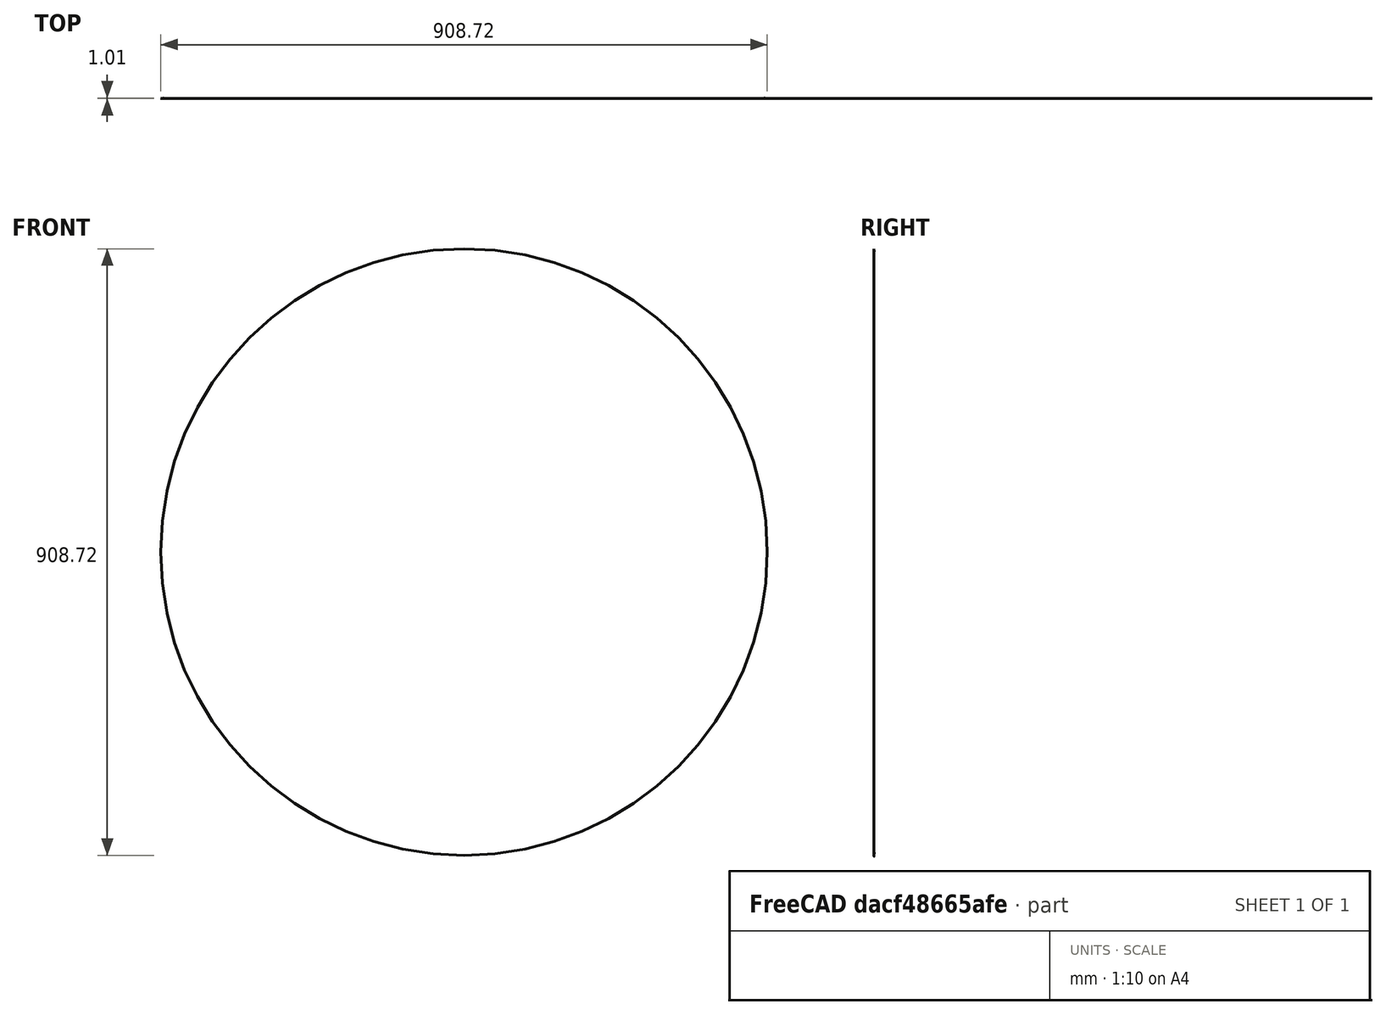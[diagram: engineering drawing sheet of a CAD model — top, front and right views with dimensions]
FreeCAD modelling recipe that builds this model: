
FCSTD DOCUMENT  (FreeCAD 0.18R16117 (Git))
Label: dish_with_rim
License: All rights reserved
LicenseURL: http://en.wikipedia.org/wiki/All_rights_reserved
objects: Sketcher::SketchObject×1, PartDesign::Revolution×1, PartDesign::Body×1, App::Part×1
note: 4 computed .brp shape members not serialized (recipe doc carries the construction recipe); baked Part::Feature solids carry a one-line shape summary decoded from their .brp

FEATURE [Sketcher::SketchObject] Sketch
  MapMode = 5
  Placement = pos=(0,0,0) rot=(0.57735,0.57735,0.57735;2.0944rad)
  Support = -> [YZ_Plane001]
  expr: Constraints[19] = Constraints.thickness
  sketch-geometry (13):
    g0: GeomPoint X=-337.5 Y=0 Z=0
    g1: ArcOfParabola CenterX=0 CenterY=0 CenterZ=0 NormalX=0 NormalY=0 NormalZ=1 Focal=337.5 AngleXU=-3.14159 StartAngle=-450 EndAngle=0
    g2: GeomPoint X=-337.5 Y=0 Z=0
    g3: LineSegment [constr] StartX=0 StartY=0 StartZ=0 EndX=-337.5 EndY=0 EndZ=0
    g4: Circle [constr] CenterX=-145.008 CenterY=453.328 CenterZ=0 NormalX=0 NormalY=0 NormalZ=1 AngleXU=0 Radius=6
    g5: GeomPoint X=-150 Y=450 Z=0
    g6: ArcOfParabola CenterX=2 CenterY=0 CenterZ=0 NormalX=0 NormalY=0 NormalZ=1 Focal=337.5 AngleXU=-3.14159 StartAngle=-454.357 EndAngle=0
    g7: GeomPoint X=-335.5 Y=0 Z=0
    g8: LineSegment [constr] StartX=2 StartY=0 StartZ=0 EndX=-335.5 EndY=0 EndZ=0
    g9: LineSegment StartX=0 StartY=0 StartZ=0 EndX=2 EndY=0 EndZ=0
    g10: GeomPoint X=-150.919 Y=454.357 Z=0
    g11: GeomPoint X=-150.919 Y=454.357 Z=0
    g12: ArcOfCircle CenterX=-145.008 CenterY=453.328 CenterZ=0 NormalX=0 NormalY=0 NormalZ=1 AngleXU=0 Radius=6 StartAngle=2.96925 EndAngle=3.7296
  constraints (30):
    c: PointOnObject(g0,g-1)
    c: InternalAlignment(g2,g1)
    c: Coincident(g2,g3)
    c: Coincident(g1,g3)
    c: Coincident(g2,g0)
    c: Coincident(g1,g-1)
    c: DistanceX(g0,g1) = 337.5
    c: DistanceY(g1,g1) = 450
    c: Horizontal(g1,g1)
    c: PointOnObject(g5,g4)
    c: Tangent(g1,g4,g5) = -1.5708
    c: Coincident(g5,g1)
    c: Diameter(g4) = 12
    c: PointOnObject(g6,g-1)
    c: InternalAlignment(g7,g6)
    c: Coincident(g7,g8)
    c: Coincident(g6,g8)
    c: PointOnObject(g7,g3)
    c: DistanceX(g1,g6) = 2  'thickness'
    c: DistanceX(g0,g7) = 2
    c: Horizontal(g6,g6)
    c: Coincident(g9,g1)
    c: Coincident(g9,g6)
    c: Coincident(g10,g11)
    c: Coincident(g10,g6)
    c: Coincident(g12,g4)
    c: Coincident(g12,g1)
    c: Coincident(g12,g6)
    c: DistanceX(g1,g1) = 150
    c: Distance(g1,g0) = 487.5
FEATURE [PartDesign::Revolution] Revolution
  Angle = 360
  Axis = (3e-16,1,-2e-16)
  Base = (0,0,0)
  Placement = pos=(0,0,0) rot=(0.57735,0.57735,0.57735;2.0944rad)
  Profile = -> Sketch
  ReferenceAxis = -> Sketch [H_Axis]
FEATURE [PartDesign::Body] Body  label="DishWithRim"
  Group = -> [Sketch,Revolution]
  Origin = -> Origin001
  Tip = -> Revolution
FEATURE [App::Part] Part
  Group = -> [Body]
  Origin = -> Origin
